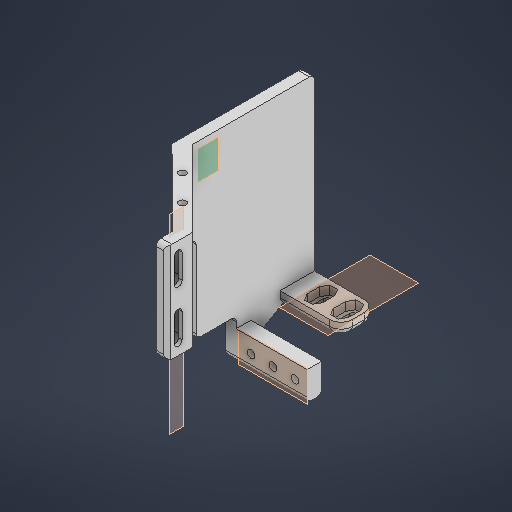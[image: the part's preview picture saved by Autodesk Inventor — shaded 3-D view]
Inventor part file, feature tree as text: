
AUTODESK INVENTOR PART (.ipt)
format: ipt  version: 2025 (Build 290162000, 162)  size: 814,080 bytes
history: native  units: mm
features: reference x38, extrude x24, sketch x21, other x9, plane x7, fillet x7, projected_geometry x5, chamfer x3, loft x1
ambient origin geometry x8: Origin, YZ Plane, XZ Plane, XY Plane, X Axis, Y Axis, Z Axis, Center Point
bodies: Solid1 (feature_tree)
feature tree (115):
  plane  "Work Plane1"
  extrude  "Extrusion1"  Depth=4.5mm TaperAngle=0.0deg
  plane  "Work Plane2"
  extrude  "Extrusion2"  Depth=2.0mm
  extrude  "Extrusion4"  Depth=3.2mm
  extrude  "Extrusion5"  Depth=6.0mm
  sketch  "Sketch7"  dims[d22=6.0mm d23=6.0mm]
  plane  "Work Plane3"
  extrude  "Extrusion6"  Depth=6.0mm
  plane  "Work Plane4"
  extrude  "Extrusion7"  Depth=6.0mm TaperAngle=0.0deg
  extrude  "Extrusion8"  Depth=6.0mm
  sketch  "Sketch10"  dims[d31=6.0mm d32=6.0mm]
  plane  "Work Plane5"
  extrude  "Extrusion9"  Depth=6.0mm
  extrude  "Extrusion10"  Depth=4.5mm
  loft  "Loft3"
  extrude  "Extrusion11"  Depth=10.58mm
  extrude  "Extrusion12"  Depth=3.0mm
  extrude  "Extrusion13"  Depth=4.5mm TaperAngle=0.0deg
  sketch  "Sketch15"  dims[d51=4.5mm d52=0.0mm d53=4.5mm d54=0.0mm]
  plane  "Work Plane6"
  extrude  "Extrusion14"  Depth=10.0mm
  fillet  "Fillet3"  Radius=24.197245mm
  sketch  "Sketch16"  dims[d55=10.0mm d56=0.0mm d57=7.218682mm d58=24.197245mm]
  extrude  "Extrusion15"  TaperAngle=0.0deg  [1 undecoded]
  extrude  "Extrusion16"  Depth=1.893mm
  extrude  "Extrusion17"  Depth=10.0mm TaperAngle=0.0deg
  extrude  "Extrusion18"  Depth=3.2mm
  chamfer  "Chamfer2"  Distance=3.2mm
  chamfer  "Chamfer3"  Distance=6.0mm
  fillet  "Fillet4"  Radius=6.0mm
  extrude  "Extrusion20"  Depth=6.0mm
  chamfer  "Chamfer4"  Distance=6.0mm
  sketch  "Sketch20"  dims[d66=10.0mm d67=0.0mm d68=10.0mm d69=0.0mm]
  extrude  "Extrusion21"  Depth=6.0mm
  extrude  "Extrusion22"  Depth=6.0mm
  fillet  "Fillet5"  Radius=3.0mm
  extrude  "Extrusion23"  Depth=10.0mm TaperAngle=0.0deg
  extrude  "Extrusion24"  Depth=2.0mm
  fillet  "Fillet6"  Radius=2.0mm
  fillet  "Fillet7"  Radius=1.5mm
  plane  "Work Plane8"
  extrude  "Extrusion27"  Depth=1.5mm
  extrude  "Extrusion28"  Depth=10.0mm
  fillet  "Fillet11"  Radius=3.2mm
  fillet  "Fillet12"  Radius=10.0mm
  sketch  "Sketch1"  dims[d0=4.5mm d1=0.0mm d2=4.5mm d3=0.0mm]
  reference  "Reference1"
  reference  "Reference2"
  reference  "Reference3"
  reference  "Reference4"
  reference  "Reference5"
  reference  "Reference6"
  reference  "Reference7"
  reference  "Reference8"
  reference  "Reference9"
  reference  "Reference10"
  reference  "Reference11"
  reference  "Reference12"
  reference  "Reference13"
  reference  "Reference14"
  reference  "Reference15"
  reference  "Reference16"
  reference  "Reference17"
  reference  "Reference18"
  reference  "Reference19"
  reference  "Reference20"
  sketch  "Sketch2"  dims[d8=2.0mm d17=3.2mm]
  reference  "Reference21"
  reference  "Reference22"
  reference  "Reference23"
  reference  "Reference24"
  reference  "Reference31"
  reference  "Reference32"
  reference  "Reference33"
  reference  "Reference34"
  sketch  "Sketch4"  dims[d18=3.2mm d19=3.2mm]
  sketch  "Sketch6"  dims[d20=3.2mm d21=6.0mm]
  projected_geometry  "Projected Loop1"
  sketch  "Sketch8"  dims[d24=6.0mm d25=3.5mm d26=0.0mm]
  reference  "Reference35"
  reference  "Reference36"
  reference  "Reference37"
  sketch  "Sketch9"  dims[d29=6.0mm d30=6.0mm]
  projected_geometry  "Projected Loop2"
  sketch  "Sketch11"  dims[d39=4.5mm d40=0.0mm d41=15.0mm]
  other  "Edges4"
  other  "Edges5"
  sketch  "Sketch12"  dims[d42=10.0mm d43=0.0mm d44=10.58mm]
  sketch  "Sketch13"  dims[d45=5.29mm d46=10.58mm]
  reference  "Reference38"
  reference  "Reference39"
  reference  "Reference40"
  sketch  "Sketch14"  dims[d47=3.0mm d48=3.0mm]
  reference  "Reference41"
  sketch  "Sketch17"  dims[d59=10.0mm d60=0.0mm d61=0.0mm d62=90.0deg]
  projected_geometry  "Projected Loop3"
  sketch  "Sketch19"  dims[d63=0.0mm d64=90.0deg d65=1.893mm]
  projected_geometry  "Projected Loop4"
  sketch  "Sketch21"  dims[d72=3.2mm d73=3.2mm]
  sketch  "Sketch22"  dims[d74=4.0mm]
  sketch  "Sketch25"  dims[d75=3.2mm]
  reference  "Reference45"
  reference  "Reference46"
  reference  "Reference47"
  sketch  "Sketch26"  dims[d76=4.0mm d77=3.2mm d78=6.0mm d79=6.0mm d80=6.0mm d81=6.0mm d82=6.0mm d83=6.0mm d84=3.0mm d85=0.0mm d93=10.0mm d94=0.0mm d96=9.0mm d97=2.0mm d98=1.5mm d100=1.5mm d102=10.0mm d103=3.2mm d104=10.0mm d105=3.2mm d106=3.0mm d107=0.0mm d108=3.0mm d109=3.0mm d110=3.0mm d111=0.0mm d112=3.0mm d113=0.0mm d114=10.0mm d115=0.0mm d116=3.0mm d117=2.0mm d118=45.0deg d123=1.5mm d124=2.0mm d125=45.0deg d126=2.0mm d127=3.0mm d128=0.0mm d129=3.0mm d130=2.0mm d131=45.0deg d132=6.0mm d133=6.0mm d134=3.0mm d135=0.0mm d136=9.0mm d137=7.5mm d138=7.5mm d139=3.0mm d140=3.0mm d141=8.0mm d142=0.0mm d143=2.0mm d144=6.0mm d145=3.0mm d146=0.0mm d147=5.0mm d148=3.2mm d149=5.0mm d150=3.2mm d151=3.0mm d152=3.0mm d153=2.725mm d154=2.725mm d155=3.5mm d156=0.0mm d157=2.725mm d158=2.0mm d159=2.0mm d168=28.0mm d169=3.1mm d170=3.1mm d171=3.1mm d172=6.0mm d173=0.0mm d174=4.5mm d175=0.0mm d176=2.0mm d177=2.0mm]
  projected_geometry  "Projected Loop5"
  other  "<userpath> 7 was better\GitHub\ReplicatorPlusConversion\CAD\Inventor\hotend-new.iam"
  other  "hotend-new.iam"
  other  "bolts reference:1"
  other  "Hemera_XS_Reference_CAD:1"
  other  "eddy:2"
  other  "hemera-xs-duct-mount-v2:1"
  other  "BL-touch:1"
note: 1 required parameter value undecoded (feature->parameter linkage not recoverable at this tier; creation-order binding heuristic only, values carry confidence <= 0.55)
